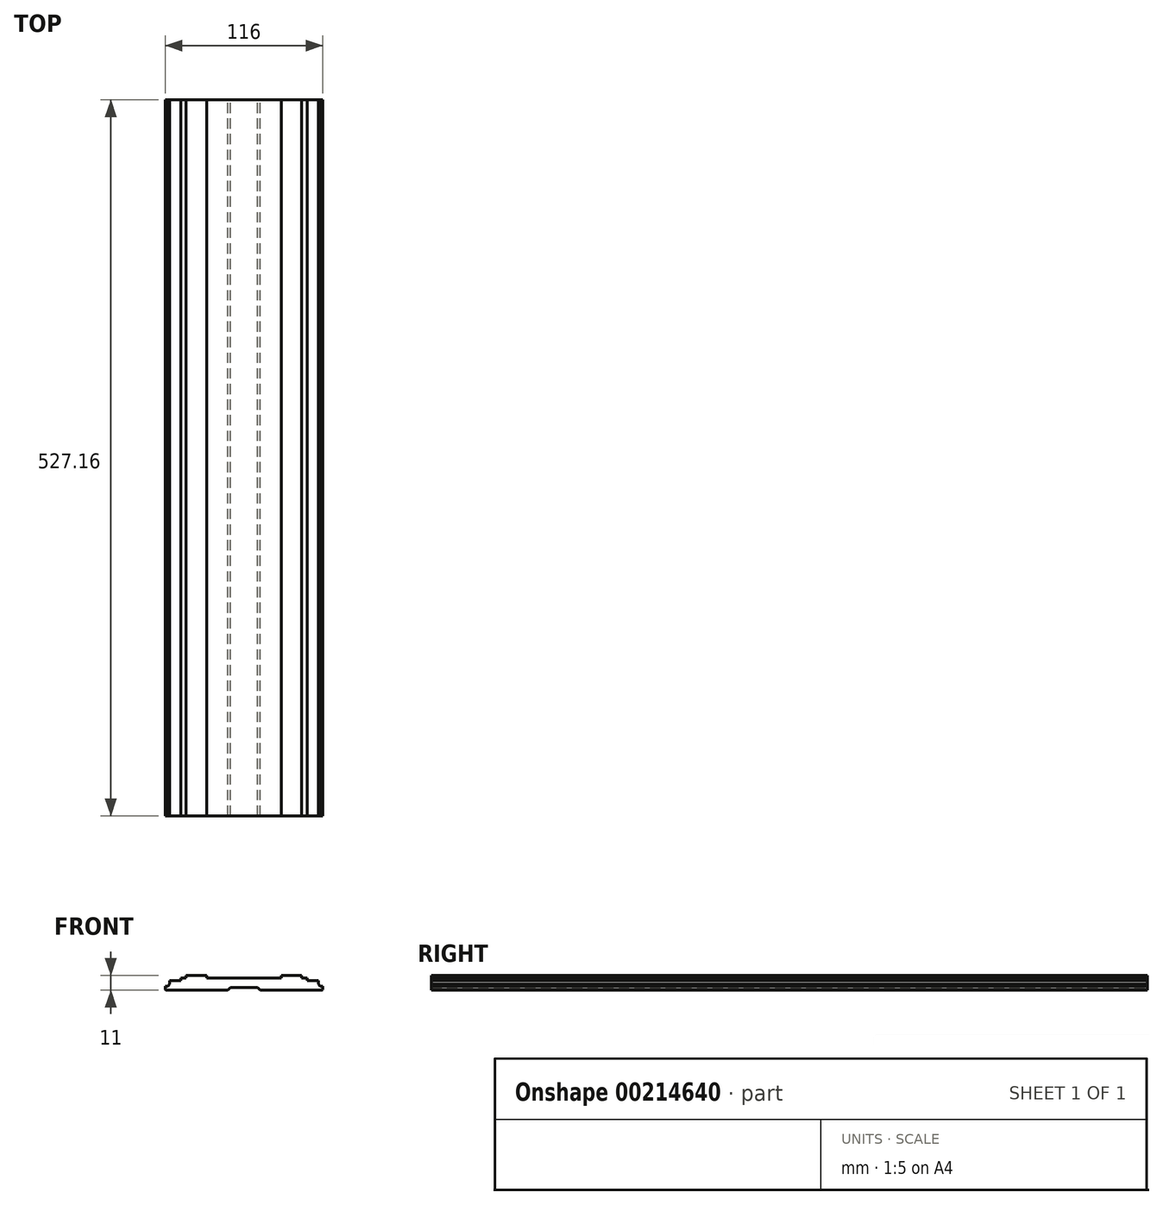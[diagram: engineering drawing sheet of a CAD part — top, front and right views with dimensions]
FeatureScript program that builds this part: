
annotation { "Feature Type Name" : "Feature", "Feature Type Description" : "" }
export const myFeature = defineFeature(function(context is Context, id is Id, definition is map)
    precondition{}
    {
        {
            var Q0;
            Q0=qCreatedBy(makeId("Front.planeOp"),FACE);
            var sketch = newSketch(context, id + "F0", { "sketchPlane" : qUnion([Q0])});
            skLineSegment(sketch, "E0", {"start": v(0, 0) * mm, "end": v(0, 60) * mm, "construction": true});
            skLineSegment(sketch, "E1", {"start": v(0, 2) * mm, "end": v(10, 2) * mm});
            skLineSegment(sketch, "E2", {"start": v(10, 2) * mm, "end": v(12, 0) * mm});
            skLineSegment(sketch, "E3", {"start": v(12, 0) * mm, "end": v(58, 0) * mm});
            skLineSegment(sketch, "E4", {"start": v(58, 0) * mm, "end": v(58, 3) * mm});
            skLineSegment(sketch, "E5", {"start": v(58, 3) * mm, "end": v(56, 3) * mm});
            skLineSegment(sketch, "E6", {"start": v(54.8, 4.7) * mm, "end": v(56, 3) * mm});
            skLineSegment(sketch, "E7", {"start": v(54.8, 4.7) * mm, "end": v(54.8, 7) * mm});
            skLineSegment(sketch, "E8", {"start": v(54.8, 7) * mm, "end": v(46.5, 7) * mm});
            skLineSegment(sketch, "E9", {"start": v(46.5, 7) * mm, "end": v(46.5, 9) * mm});
            skLineSegment(sketch, "E10", {"start": v(46.5, 9) * mm, "end": v(42.5, 9) * mm});
            skLineSegment(sketch, "E11", {"start": v(42.5, 9) * mm, "end": v(42.5, 11) * mm});
            skLineSegment(sketch, "E12", {"start": v(42.5, 11) * mm, "end": v(27.5, 11) * mm});
            skLineSegment(sketch, "E13", {"start": v(27.5, 11) * mm, "end": v(27.5, 9) * mm});
            skLineSegment(sketch, "E14", {"start": v(27.5, 9) * mm, "end": v(0, 9) * mm});
            skLineSegment(sketch, "E15.MirrorCS", {"start": v(-10, 2) * mm, "end": v(-12, 0) * mm});
            skLineSegment(sketch, "E16.MirrorCS", {"start": v(-27.5, 11) * mm, "end": v(-27.5, 9) * mm});
            skLineSegment(sketch, "E17.MirrorCS", {"start": v(-42.5, 9) * mm, "end": v(-42.5, 11) * mm});
            skLineSegment(sketch, "E18.MirrorCS", {"start": v(-58, 3) * mm, "end": v(-56, 3) * mm});
            skLineSegment(sketch, "E19.MirrorCS", {"start": v(-46.5, 7) * mm, "end": v(-46.5, 9) * mm});
            skLineSegment(sketch, "E20.MirrorCS", {"start": v(-54.8, 4.7) * mm, "end": v(-54.8, 7) * mm});
            skLineSegment(sketch, "E21.MirrorCS", {"start": v(-54.8, 4.7) * mm, "end": v(-56, 3) * mm});
            skLineSegment(sketch, "E22.MirrorCS", {"start": v(-27.5, 9) * mm, "end": v(0, 9) * mm});
            skLineSegment(sketch, "E23.MirrorCS", {"start": v(0, 2) * mm, "end": v(-10, 2) * mm});
            skLineSegment(sketch, "E24.MirrorCS", {"start": v(-42.5, 11) * mm, "end": v(-27.5, 11) * mm});
            skLineSegment(sketch, "E25.MirrorCS", {"start": v(-54.8, 7) * mm, "end": v(-46.5, 7) * mm});
            skLineSegment(sketch, "E26.MirrorCS", {"start": v(-46.5, 9) * mm, "end": v(-42.5, 9) * mm});
            skLineSegment(sketch, "E27.MirrorCS", {"start": v(-12, 0) * mm, "end": v(-58, 0) * mm});
            skLineSegment(sketch, "E28.MirrorCS", {"start": v(-58, 0) * mm, "end": v(-58, 3) * mm});
            skSolve(sketch);
        }
        {
            var Q0;
            Q0=makeQuery(id+"F0.imprint","IMPRINT",FACE,{"disambiguationData":[TD([[makeQuery(id+"F0.imprint","IMPRINT",EDGE,{"derivedFrom":sQuery(id+"F0.wireOp",EDGE,"E1")}),1.0]])]});
            extrude(context, id + "F1", {"entities" : qUnion([Q0]), "endBound" : BoundingType.SYMMETRIC, "depth" : 527.17 * mm});
        }
        {
            var Q0;
            Q0=makeQuery(id+"F1.opExtrude","SWEPT_EDGE",EDGE,{"disambiguationData":[OSD([sQuery(id+"F0.wireOp",EDGE,"E3"),sQuery(id+"F0.wireOp",EDGE,"E4")])]});
            var Q1;
            Q1=makeQuery(id+"F1.opExtrude","SWEPT_EDGE",EDGE,{"disambiguationData":[OSD([sQuery(id+"F0.wireOp",EDGE,"E27.MirrorCS"),sQuery(id+"F0.wireOp",EDGE,"E28.MirrorCS")])]});
            chamfer(context, id + "F2", {"entities" : qUnion([Q0, Q1]), "width" : .5 * mm, "tangentPropagation" : true});
        }
    });
